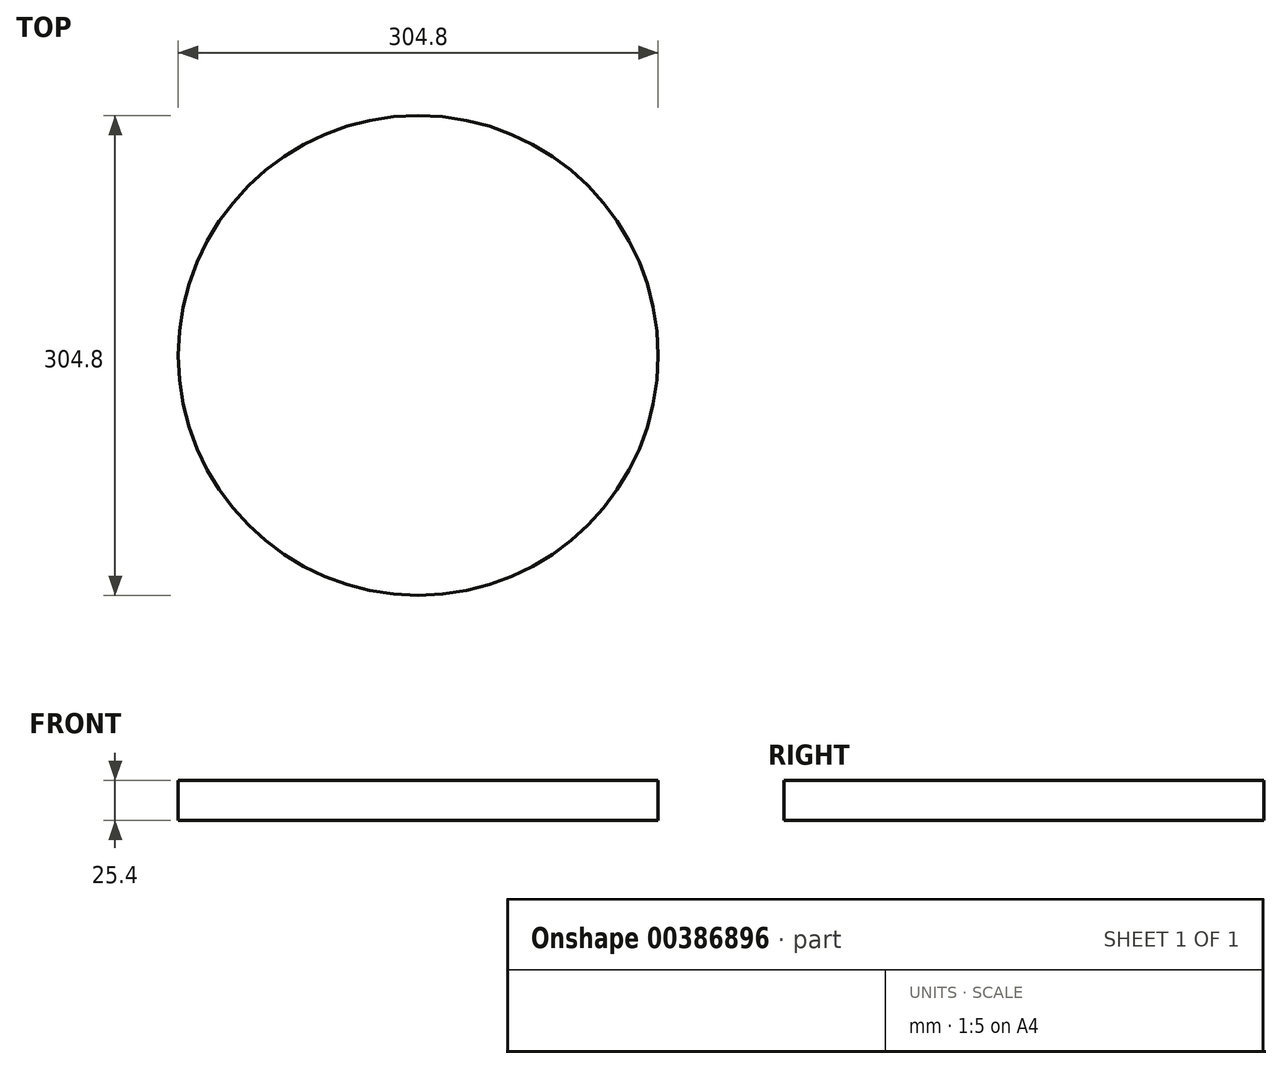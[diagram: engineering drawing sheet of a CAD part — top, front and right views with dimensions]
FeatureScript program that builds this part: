
annotation { "Feature Type Name" : "Feature", "Feature Type Description" : "" }
export const myFeature = defineFeature(function(context is Context, id is Id, definition is map)
    precondition{}
    {
        {
            var Q0;
            Q0=qCreatedBy(makeId("Top.planeOp"),FACE);
            var sketch = newSketch(context, id + "F0", { "sketchPlane" : qUnion([Q0])});
            skCircle(sketch, "E0", {"center": v(0, 0) * mm, "radius": 152.4 * mm});
            skSolve(sketch);
        }
        {
            var Q0;
            Q0=makeQuery(id+"F0.imprint","IMPRINT",FACE,{"disambiguationData":[TD([[makeQuery(id+"F0.imprint","IMPRINT",EDGE,{"derivedFrom":sQuery(id+"F0.wireOp",EDGE,"E0")}),1.0]])]});
            extrude(context, id + "F1", {"entities" : qUnion([Q0]), "depth" : 25.4 * mm});
        }
    });
